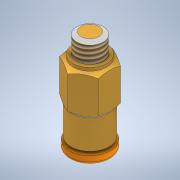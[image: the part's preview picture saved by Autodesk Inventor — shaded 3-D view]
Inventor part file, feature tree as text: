
AUTODESK INVENTOR PART (.ipt)
format: ipt  version: 2021 (Build 250183000, 183)  size: 205,312 bytes
history: native  units: mm
features: extrude x7, sketch x7, chamfer x3, fillet x2, thread x1
ambient origin geometry x8: Origin, YZ Plane, XZ Plane, XY Plane, X Axis, Y Axis, Z Axis, Center Point
bodies: Solid1 (feature_tree)
feature tree (20):
  extrude  "Extrusion1"  Depth=7.0mm TaperAngle=0.0deg
  chamfer  "Chamfer1"  Distance=1.0mm Angle=30.0deg
  chamfer  "Chamfer2"  Distance=1.0mm Angle=30.0deg
  extrude  "Extrusion2"  Depth=7.0mm
  extrude  "Extrusion3"  Depth=0.5mm
  fillet  "Fillet1"  Radius=4.5mm
  extrude  "Extrusion4"  Depth=0.5mm
  extrude  "Extrusion5"  Depth=0.5mm
  fillet  "Fillet2"  Radius=0.6mm
  extrude  "Extrusion6"  Depth=3.5mm TaperAngle=0.0deg
  extrude  "Extrusion7"  Depth=0.8mm TaperAngle=30.0deg
  thread  "Thread1"  [1 undecoded]
  chamfer  "Chamfer3"  [1 undecoded]
  sketch  "Sketch1"  dims[d0=7.0mm d1=7.0mm d2=0.0mm d3=1.0mm d4=2.0mm d5=30.0deg d6=1.0mm d7=2.0mm d8=30.0deg]
  sketch  "Sketch2"  dims[d9=7.0mm d10=0.0mm d11=6.9mm]
  sketch  "Sketch3"  dims[d12=5.3mm d13=0.0mm d14=0.5mm d15=4.5mm]
  sketch  "Sketch4"  dims[d16=0.5mm d17=0.0mm d18=7.4mm]
  sketch  "Sketch5"  dims[d19=1.5mm d20=0.0mm d21=0.5mm d22=0.6mm d23=0.0mm]
  sketch  "Sketch6"  dims[d24=4.826mm d25=3.5mm d26=0.0mm]
  sketch  "Sketch7"  dims[d27=15.103mm d28=0.0mm d29=0.8mm d30=2.0mm d31=30.0deg]
note: 2 required parameter values undecoded (feature->parameter linkage not recoverable at this tier; creation-order binding heuristic only, values carry confidence <= 0.55)
